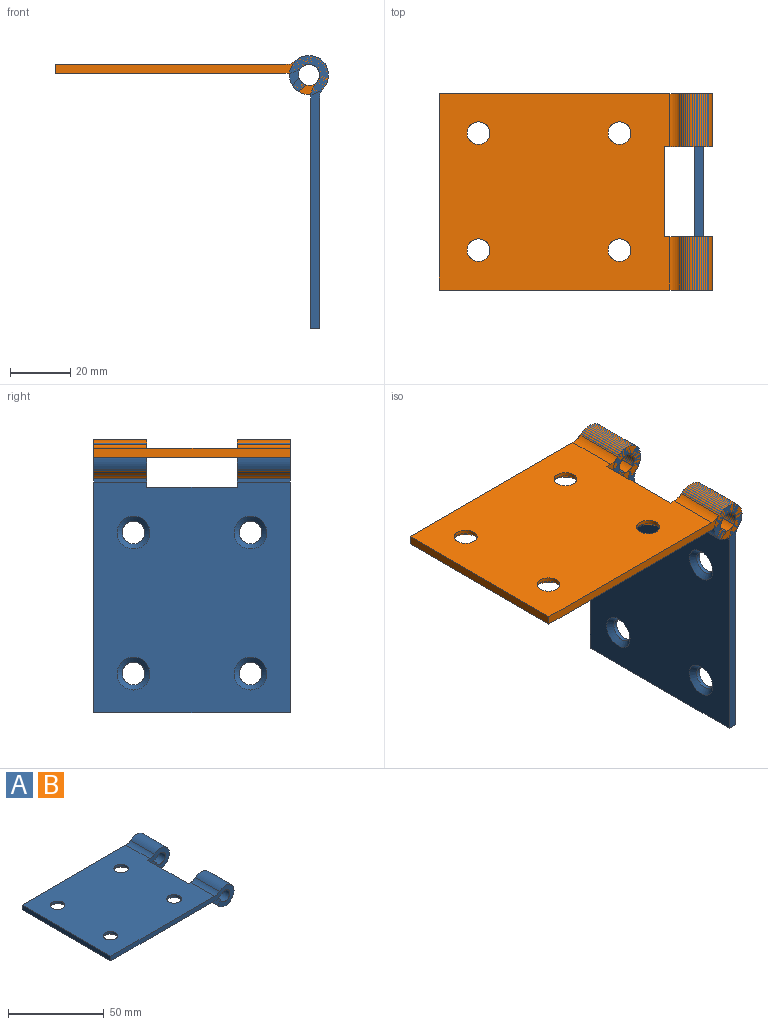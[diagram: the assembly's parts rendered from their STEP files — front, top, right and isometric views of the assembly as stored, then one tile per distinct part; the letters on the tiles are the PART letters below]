
ASSEMBLY  parts=2 mates=1
PART A: 26 faces, bbox 91x65.5x13 mm
  f0: cylinder r=5mm len=17.75mm, axis (0,1,0), area 65.6mm2, adj f1,f6,f14,f16
  f1: plane 76.75x65.5mm, normal (0,0,1), area 4793.3mm2, adj f0,f7,f8,f13,f14,f15,f16,f17
  f2: plane 76.75x65.5mm, normal (0,0,-1), area 4594.6mm2, adj f3,f8,f9,f13,f14,f15,f16,f17
  f3: cylinder r=8mm len=17.75mm, axis (0,1,0), area 104.9mm2, adj f2,f4,f14,f16
  f4: cylinder r=3.5mm len=17.75mm, axis (0,1,0), area 324.2mm2, adj f3,f5,f14,f16
  f5: plane 17.75x2.69mm, normal (-0.79,0,0.61), area 60.3mm2, adj f4,f6,f14,f16
  f6: cylinder r=6.5mm len=17.75mm, axis (0,1,0), area 563.4mm2, adj f0,f5,f14,f16
  f7: cylinder r=5mm len=17.75mm, axis (0,1,0), area 65.6mm2, adj f1,f12,f13,f17
  f8: plane 65.5x3mm, normal (-1,0,0), area 196.5mm2, adj f1,f2,f13,f14
  f9: cylinder r=8mm len=17.75mm, axis (0,1,0), area 104.9mm2, adj f2,f10,f13,f17
  f10: cylinder r=3.5mm len=17.75mm, axis (0,1,0), area 324.2mm2, adj f9,f11,f13,f17
  f11: plane 17.75x2.69mm, normal (-0.79,0,0.61), area 60.3mm2, adj f10,f12,f13,f17
  f12: cylinder r=6.5mm len=17.75mm, axis (0,1,0), area 563.4mm2, adj f7,f11,f13,f17
  f13: plane 91x13mm, normal (0,-1,0), area 319.6mm2, adj f1,f2,f7,f8,f9,f10,f11,f12
  f14: plane 91x13mm, normal (0,1,0), area 319.6mm2, adj f0,f1,f2,f3,f4,f5,f6,f8
  f15: plane 30x3mm, normal (1,0,0), area 90mm2, adj f1,f2,f16,f17
  f16: plane 16x13mm, normal (0,-1,0), area 94.6mm2, adj f0,f1,f2,f3,f4,f5,f6,f15
  f17: plane 16x13mm, normal (0,1,0), area 94.6mm2, adj f1,f2,f7,f9,f10,f11,f12,f15
  f18: cylinder r=3.8mm len=7.6mm, axis (0,0,-1), area 31mm2, adj f1,f19
  f19: cone r=3.8mm half-angle=45deg, axis (0,0,-1), area 70.2mm2, adj f2,f18
  f20: cylinder r=3.8mm len=7.6mm, axis (0,0,-1), area 31mm2, adj f1,f21
  f21: cone r=3.8mm half-angle=45deg, axis (0,0,-1), area 70.2mm2, adj f2,f20
  f22: cylinder r=3.8mm len=7.6mm, axis (0,0,-1), area 31mm2, adj f1,f23
  f23: cone r=3.8mm half-angle=45deg, axis (0,0,-1), area 70.2mm2, adj f2,f22
  f24: cylinder r=3.8mm len=7.6mm, axis (0,0,-1), area 31mm2, adj f1,f25
  f25: cone r=3.8mm half-angle=45deg, axis (0,0,-1), area 70.2mm2, adj f2,f24
PART B: same geometry as A
PLACE A rot(axis=(0.71,0,0.71),180deg) t=(0,0,0)mm
PLACE B at identity fixed
MATE revolute B.f6 <-> A.f6  axis (0,-1,0) through (0,15,0)mm
